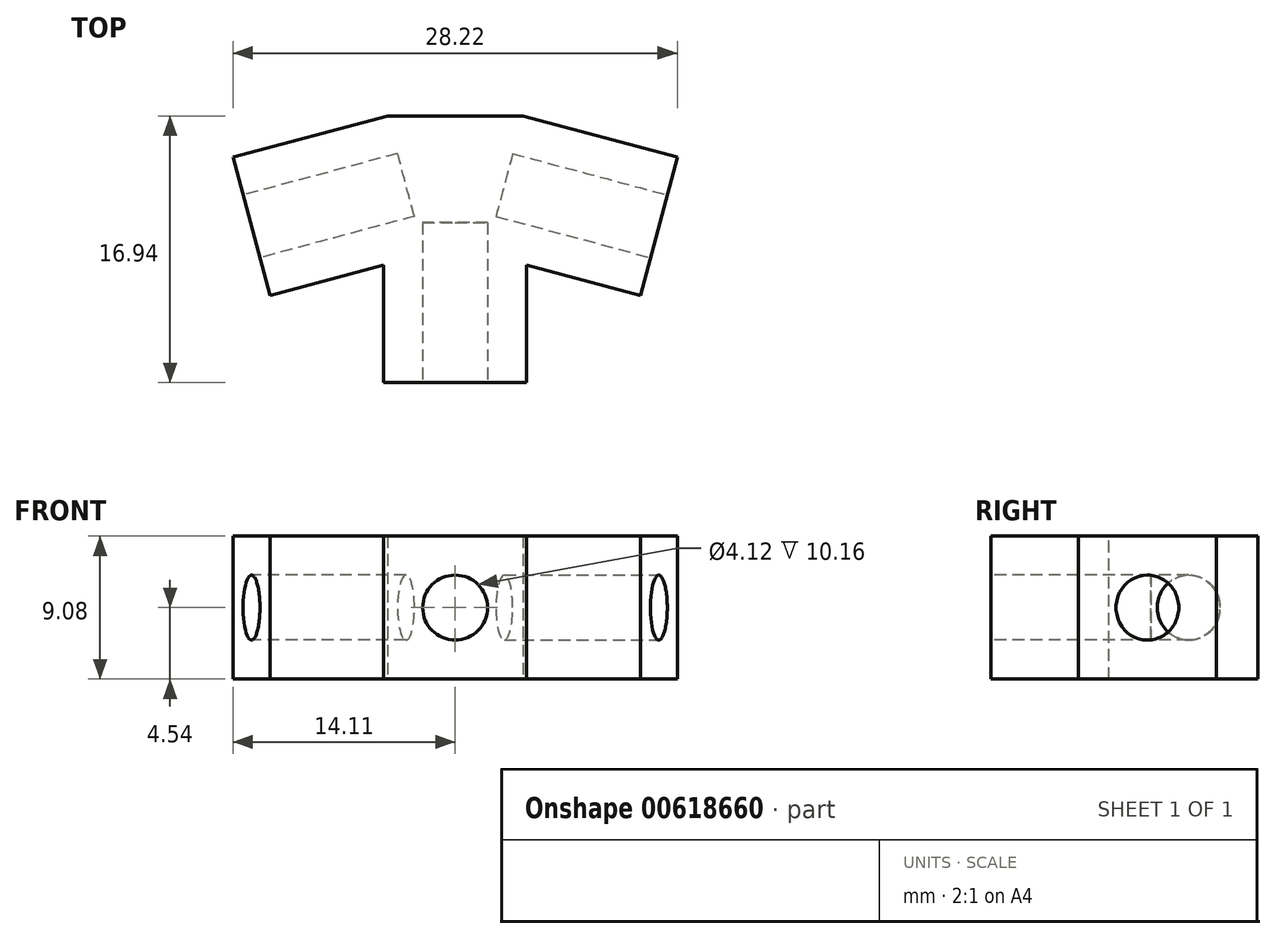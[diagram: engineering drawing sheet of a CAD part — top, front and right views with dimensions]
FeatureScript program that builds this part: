
annotation { "Feature Type Name" : "Feature", "Feature Type Description" : "" }
export const myFeature = defineFeature(function(context is Context, id is Id, definition is map)
    precondition{}
    {
        {
            var Q0;
            Q0=qCreatedBy(makeId("Top.planeOp"),FACE);
            var sketch = newSketch(context, id + "F0", { "sketchPlane" : qUnion([Q0])});
            skLineSegment(sketch, "E0", {"start": v(0, 0) * mm, "end": v(0, -13.4) * mm, "construction": true});
            skLineSegment(sketch, "E1", {"start": v(0, 0) * mm, "end": v(12.94, -3.47) * mm, "construction": true});
            skLineSegment(sketch, "E2", {"start": v(0, 0) * mm, "end": v(-12.94, -3.47) * mm, "construction": true});
            skLineSegment(sketch, "E3", {"start": v(-3.12, -0.84) * mm, "end": v(-3.64, 1.1) * mm, "construction": true});
            skLineSegment(sketch, "E4", {"start": v(-3.12, -0.84) * mm, "end": v(-2.6, -2.77) * mm, "construction": true});
            skLineSegment(sketch, "E5.bottom", {"start": v(-2, -3.23) * mm, "end": v(2, -3.23) * mm, "construction": true});
            skLineSegment(sketch, "E5.top", {"start": v(-2, -13.4) * mm, "end": v(2, -13.4) * mm, "construction": true});
            skLineSegment(sketch, "E5.left", {"start": v(-2, -3.23) * mm, "end": v(-2, -13.4) * mm, "construction": true});
            skLineSegment(sketch, "E5.right", {"start": v(2, -3.23) * mm, "end": v(2, -13.4) * mm, "construction": true});
            skPoint(sketch, "E5.middle", {"position": v(0, -8.31) * mm});
            skLineSegment(sketch, "E6", {"start": v(0, 0) * mm, "end": v(-8.15, -10.62) * mm, "construction": true});
            skLineSegment(sketch, "E7", {"start": v(-2.6, -2.77) * mm, "end": v(-2, -3.23) * mm, "construction": true});
            skLineSegment(sketch, "E8", {"start": v(0, 4.7) * mm, "end": v(-14.11, 0.92) * mm});
            skLineSegment(sketch, "E9", {"start": v(-14.11, 0.92) * mm, "end": v(-12.94, -3.47) * mm});
            skLineSegment(sketch, "E10", {"start": v(-12.94, -3.47) * mm, "end": v(-11.76, -7.85) * mm});
            skLineSegment(sketch, "E11", {"start": v(0, -13.4) * mm, "end": v(-4.54, -13.4) * mm});
            skLineSegment(sketch, "E12", {"start": v(0, -13.4) * mm, "end": v(4.54, -13.4) * mm});
            skLineSegment(sketch, "E13", {"start": v(12.94, -3.47) * mm, "end": v(11.76, -7.85) * mm});
            skLineSegment(sketch, "E14", {"start": v(12.94, -3.47) * mm, "end": v(14.11, 0.92) * mm});
            skLineSegment(sketch, "E15", {"start": v(0, 4.7) * mm, "end": v(14.11, 0.92) * mm});
            skLineSegment(sketch, "E16", {"start": v(-11.76, -7.85) * mm, "end": v(-4.54, -13.4) * mm});
            skLineSegment(sketch, "E17", {"start": v(4.54, -13.4) * mm, "end": v(11.76, -7.85) * mm});
            skLineSegment(sketch, "E18", {"start": v(-3.64, 1.1) * mm, "end": v(-4.3, 3.55) * mm, "construction": true});
            skLineSegment(sketch, "E19", {"start": v(-4.3, 3.55) * mm, "end": v(4.3, 3.55) * mm});
            skSolve(sketch);
        }
        {
            var Q0;
            {var subQ3=sQuery(id+"F0.wireOp",EDGE,"E9");Q0=makeQuery(id+"F0.imprint","IMPRINT",FACE,{"disambiguationData":[TD([[makeQuery(id+"F0.imprint","IMPRINT",EDGE,{"derivedFrom":subQ3}),1.0]])]});}
            extrude(context, id + "F1", {"entities" : qUnion([Q0]), "endBound" : BoundingType.SYMMETRIC, "depth" : 5.08 * mm + 4 * mm, "offsetDistance" : 25.4 * mm});
        }
        {
            var Q0;
            Q0=makeQuery(id+"F1.opExtrude","SWEPT_FACE",FACE,{"disambiguationData":[OSD([sQuery(id+"F0.wireOp",EDGE,"E9"),sQuery(id+"F0.wireOp",EDGE,"E10")])]});
            var sketch = newSketch(context, id + "F2", { "sketchPlane" : qUnion([Q0])});
            skPoint(sketch, "E20.0", {"position": v(0, 0) * mm});
            skCircle(sketch, "E21", {"center": v(0, 0) * mm, "radius": 2.06 * mm});
            skSolve(sketch);
        }
        {
            var Q0;
            Q0 = qSketchRegion(id + "F2", true);
            extrude(context, id + "F3", {"entities" : qUnion([Q0]), "operationType" : NewBodyOperationType.REMOVE, "oppositeDirection" : true, "depth" : 10.16 * mm, "offsetDistance" : 25.4 * mm});
        }
        {
            var Q0;
            Q0=makeQuery(id+"F1.opExtrude","SWEPT_FACE",FACE,{"disambiguationData":[OSD([sQuery(id+"F0.wireOp",EDGE,"E11"),sQuery(id+"F0.wireOp",EDGE,"E12")])]});
            var sketch = newSketch(context, id + "F4", { "sketchPlane" : qUnion([Q0])});
            skPoint(sketch, "E22.0", {"position": v(0, 0) * mm});
            skCircle(sketch, "E23", {"center": v(0, 0) * mm, "radius": 2.06 * mm});
            skSolve(sketch);
        }
        {
            var Q0;
            Q0=makeQuery(id+"F4.imprint","IMPRINT",FACE,{"disambiguationData":[TD([[makeQuery(id+"F4.imprint","IMPRINT",EDGE,{"derivedFrom":sQuery(id+"F4.wireOp",EDGE,"E23")}),1.0]])]});
            extrude(context, id + "F5", {"entities" : qUnion([Q0]), "operationType" : NewBodyOperationType.REMOVE, "oppositeDirection" : true, "depth" : 10.16 * mm, "offsetDistance" : 25.4 * mm});
        }
        {
            var Q0;
            Q0=makeQuery(id+"F1.opExtrude","SWEPT_FACE",FACE,{"disambiguationData":[OSD([sQuery(id+"F0.wireOp",EDGE,"E13"),sQuery(id+"F0.wireOp",EDGE,"E14")])]});
            var sketch = newSketch(context, id + "F6", { "sketchPlane" : qUnion([Q0])});
            skPoint(sketch, "E24.0", {"position": v(0, 0) * mm});
            skCircle(sketch, "E25", {"center": v(0, 0) * mm, "radius": 2.06 * mm});
            skSolve(sketch);
        }
        {
            var Q0;
            Q0 = qSketchRegion(id + "F6", true);
            extrude(context, id + "F7", {"entities" : qUnion([Q0]), "operationType" : NewBodyOperationType.REMOVE, "oppositeDirection" : true, "depth" : 10.16 * mm, "offsetDistance" : 25.4 * mm});
        }
        {
            var Q0;
            Q0=makeQuery(id+"F1.opExtrude","CAP_FACE",FACE,{"disambiguationData":[OSD([sQuery(id+"F0.wireOp",EDGE,"E8"),sQuery(id+"F0.wireOp",EDGE,"E9"),sQuery(id+"F0.wireOp",EDGE,"E10"),sQuery(id+"F0.wireOp",EDGE,"E11"),sQuery(id+"F0.wireOp",EDGE,"E12"),sQuery(id+"F0.wireOp",EDGE,"E13"),sQuery(id+"F0.wireOp",EDGE,"E14"),sQuery(id+"F0.wireOp",EDGE,"E15"),sQuery(id+"F0.wireOp",EDGE,"E16"),sQuery(id+"F0.wireOp",EDGE,"E17"),sQuery(id+"F0.wireOp",EDGE,"E19")])],"isStart":false});
            var sketch = newSketch(context, id + "F8", { "sketchPlane" : qUnion([Q0])});
            skLineSegment(sketch, "E26.0.0", {"start": v(14.11, 0.92) * mm, "end": v(4.3, 3.55) * mm});
            skLineSegment(sketch, "E26.0.1", {"start": v(4.3, 3.55) * mm, "end": v(-4.3, 3.55) * mm});
            skLineSegment(sketch, "E26.0.2", {"start": v(-4.3, 3.55) * mm, "end": v(-14.11, 0.92) * mm});
            skLineSegment(sketch, "E26.0.3", {"start": v(-14.11, 0.92) * mm, "end": v(-11.76, -7.85) * mm});
            skLineSegment(sketch, "E26.0.4", {"start": v(-11.76, -7.85) * mm, "end": v(-4.54, -13.4) * mm});
            skLineSegment(sketch, "E26.0.5", {"start": v(-4.54, -13.4) * mm, "end": v(4.54, -13.4) * mm});
            skLineSegment(sketch, "E26.0.6", {"start": v(4.54, -13.4) * mm, "end": v(11.76, -7.85) * mm});
            skLineSegment(sketch, "E26.0.7", {"start": v(11.76, -7.85) * mm, "end": v(14.11, 0.92) * mm});
            skLineSegment(sketch, "E27", {"start": v(-11.76, -7.85) * mm, "end": v(-4.54, -5.92) * mm});
            skLineSegment(sketch, "E28", {"start": v(-4.54, -5.92) * mm, "end": v(-4.54, -13.4) * mm});
            skLineSegment(sketch, "E29", {"start": v(4.54, -13.4) * mm, "end": v(4.54, -5.92) * mm});
            skLineSegment(sketch, "E30", {"start": v(4.54, -5.92) * mm, "end": v(11.76, -7.85) * mm});
            skSolve(sketch);
        }
        {
            var Q0;
            Q0=makeQuery(id+"F8.imprint","IMPRINT",FACE,{"disambiguationData":[TD([[makeQuery(id+"F8.imprint","IMPRINT",EDGE,{"derivedFrom":sQuery(id+"F8.wireOp",EDGE,"E26.0.6")}),1.0]])]});
            var Q1;
            Q1=makeQuery(id+"F8.imprint","IMPRINT",FACE,{"disambiguationData":[TD([[makeQuery(id+"F8.imprint","IMPRINT",EDGE,{"derivedFrom":sQuery(id+"F8.wireOp",EDGE,"E26.0.4")}),1.0]])]});
            extrude(context, id + "F9", {"entities" : qUnion([Q0, Q1]), "operationType" : NewBodyOperationType.REMOVE, "endBound" : BoundingType.THROUGH_ALL, "oppositeDirection" : true, "depth" : 25.4 * mm, "offsetDistance" : 25.4 * mm});
        }
    });
